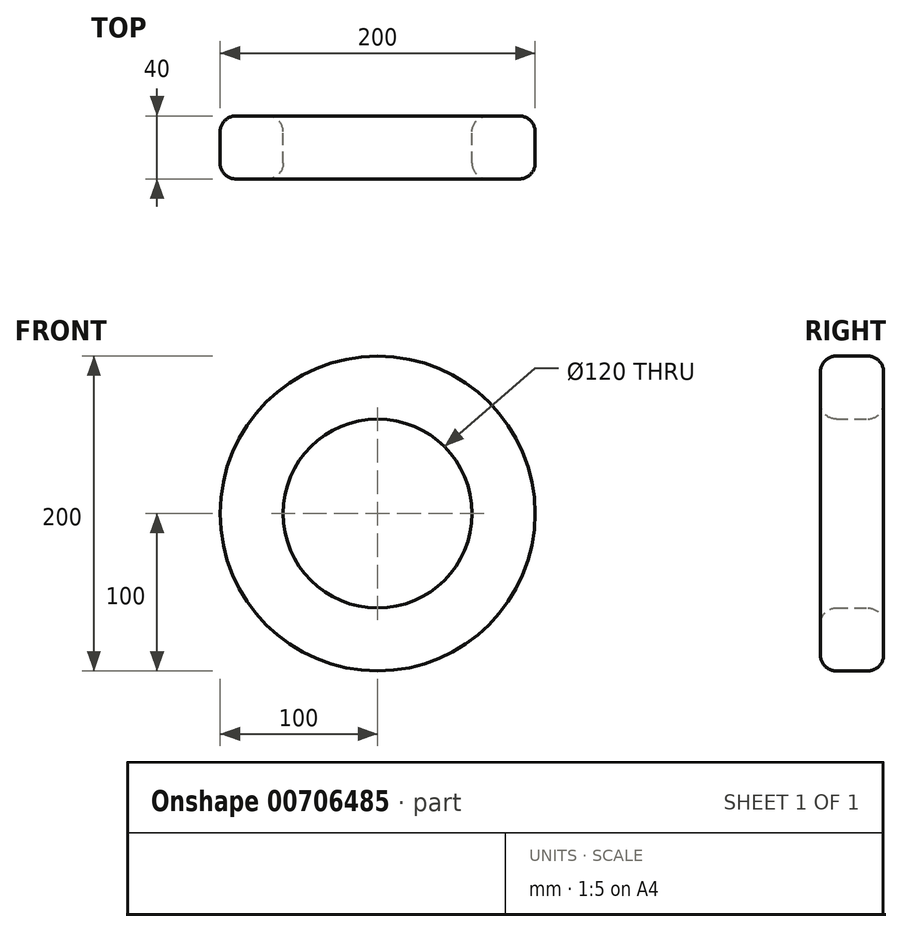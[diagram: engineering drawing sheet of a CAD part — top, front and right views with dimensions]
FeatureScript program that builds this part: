
annotation { "Feature Type Name" : "Feature", "Feature Type Description" : "" }
export const myFeature = defineFeature(function(context is Context, id is Id, definition is map)
    precondition{}
    {
        {
            var Q0;
            Q0=qCreatedBy(makeId("Front.planeOp"),FACE);
            var sketch = newSketch(context, id + "F0", { "sketchPlane" : qUnion([Q0])});
            skCircle(sketch, "E0", {"center": v(0, 0) * mm, "radius": 100 * mm});
            skCircle(sketch, "E1", {"center": v(0, 0) * mm, "radius": 60 * mm});
            skSolve(sketch);
        }
        {
            var Q0;
            Q0=makeQuery(id+"F0.imprint","IMPRINT",FACE,{"disambiguationData":[TD([[makeQuery(id+"F0.imprint","IMPRINT",EDGE,{"derivedFrom":sQuery(id+"F0.wireOp",EDGE,"E0")}),1.0]])]});
            extrude(context, id + "F1", {"entities" : qUnion([Q0]), "depth" : 40 * mm, "offsetDistance" : 25 * mm});
        }
        {
            var Q0;
            Q0=makeQuery(id+"F1.opExtrude","CAP_EDGE",EDGE,{"disambiguationData":[OSD([sQuery(id+"F0.wireOp",EDGE,"E0")])],"isStart":false});
            var Q1;
            Q1=makeQuery(id+"F1.opExtrude","CAP_EDGE",EDGE,{"disambiguationData":[OSD([sQuery(id+"F0.wireOp",EDGE,"E1")])],"isStart":false});
            var Q2;
            Q2=makeQuery(id+"F1.opExtrude","CAP_EDGE",EDGE,{"disambiguationData":[OSD([sQuery(id+"F0.wireOp",EDGE,"E0")])],"isStart":true});
            var Q3;
            Q3=makeQuery(id+"F1.opExtrude","CAP_EDGE",EDGE,{"disambiguationData":[OSD([sQuery(id+"F0.wireOp",EDGE,"E1")])],"isStart":true});
            fillet(context, id + "F2", {"entities" : qUnion([Q0, Q1, Q2, Q3]), "radius" : 10 * mm, "tangentPropagation" : true, "allowEdgeOverflow" : false});
        }
    });
